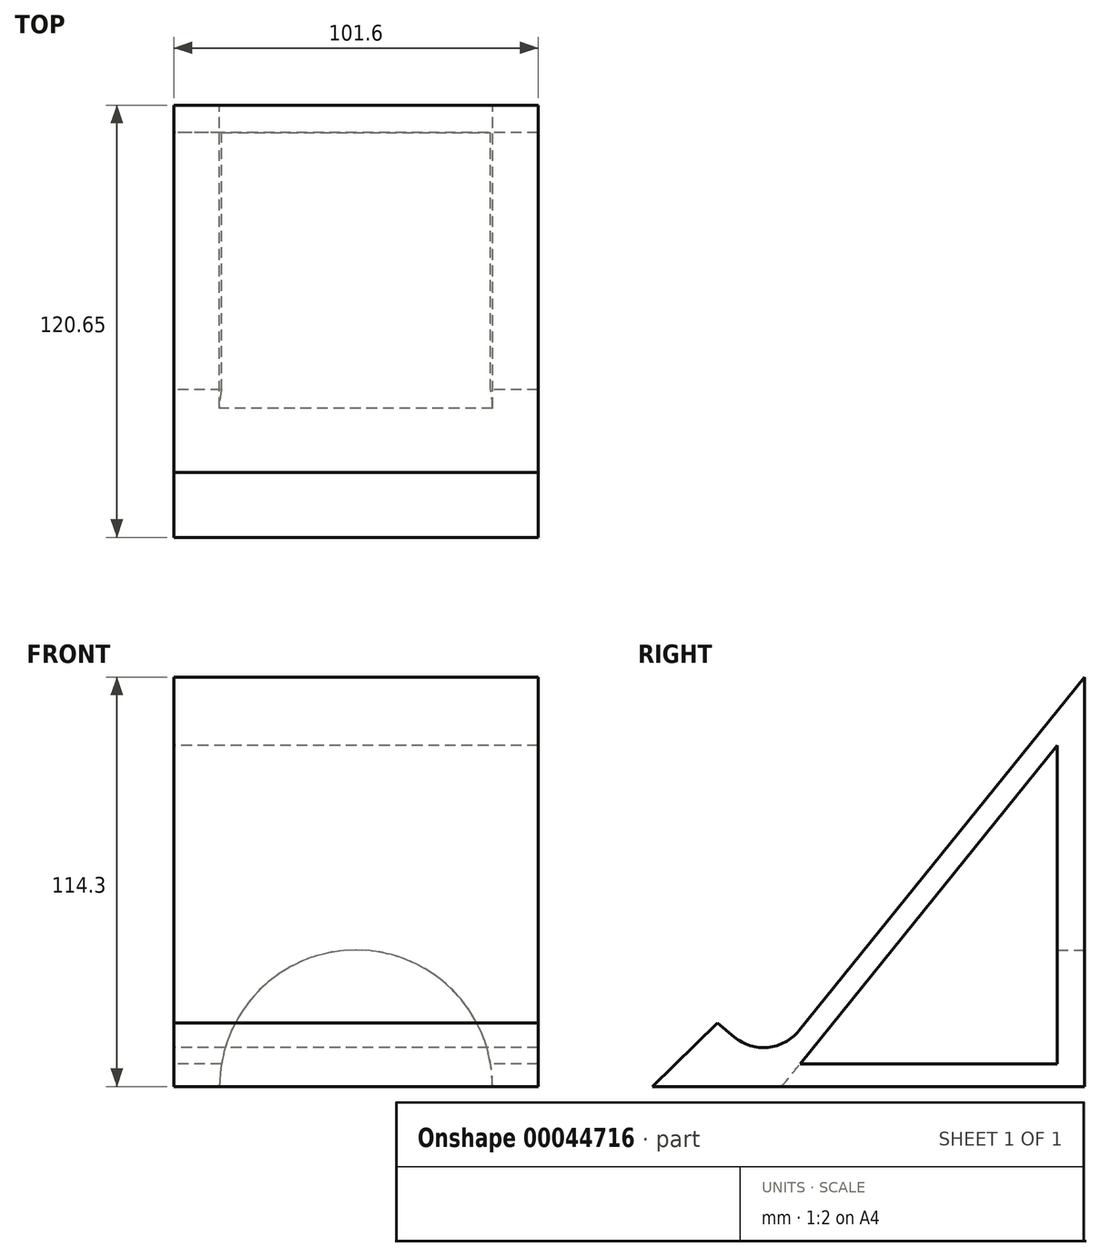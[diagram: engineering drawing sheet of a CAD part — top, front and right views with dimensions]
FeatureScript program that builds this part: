
annotation { "Feature Type Name" : "Feature", "Feature Type Description" : "" }
export const myFeature = defineFeature(function(context is Context, id is Id, definition is map)
    precondition{}
    {
        {
            var Q0;
            Q0=qCreatedBy(makeId("Right.planeOp"),FACE);
            var sketch = newSketch(context, id + "F0", { "sketchPlane" : qUnion([Q0])});
            skLineSegment(sketch, "E0", {"start": v(-54.33, -41.01) * mm, "end": v(66.32, -41.01) * mm});
            skLineSegment(sketch, "E1", {"start": v(66.32, -41.01) * mm, "end": v(66.32, 73.29) * mm});
            skLineSegment(sketch, "E2", {"start": v(-54.33, -41.01) * mm, "end": v(-36.18, -23.25) * mm});
            skLineSegment(sketch, "E3", {"start": v(-36.18, -23.25) * mm, "end": v(-31.51, -27.17) * mm});
            skLineSegment(sketch, "E4", {"start": v(-13.46, -25.44) * mm, "end": v(66.32, 73.29) * mm});
            skPoint(sketch, "E5.visualSharp", {"position": v(-21.6, -35.51) * mm});
            skArc(sketch, "E5.filletArc", {"start": v(-31.51, -27.17) * mm, "mid": v(-22.12, -30.1) * mm, "end": v(-13.46, -25.44) * mm});
            skLineSegment(sketch, "E6", {"start": v(-13.14, -34.66) * mm, "end": v(58.7, 54.24) * mm});
            skLineSegment(sketch, "E7", {"start": v(58.7, 54.24) * mm, "end": v(58.7, -34.66) * mm});
            skLineSegment(sketch, "E8", {"start": v(-13.14, -34.66) * mm, "end": v(58.7, -34.66) * mm});
            skLineSegment(sketch, "E9", {"start": v(58.7, 54.24) * mm, "end": v(66.32, 54.24) * mm});
            skLineSegment(sketch, "E10", {"start": v(58.7, -34.66) * mm, "end": v(58.7, -41.01) * mm});
            skSolve(sketch);
        }
        {
            var Q0;
            Q0 = qSketchRegion(id + "F0", true);
            extrude(context, id + "F1", {"entities" : qUnion([Q0]), "depth" : 101.6 * mm});
        }
        {
            var Q0;
            Q0=makeQuery(id+"F1.opExtrude","SWEPT_FACE",FACE,{"disambiguationData":[OSD([sQuery(id+"F0.wireOp",EDGE,"E1")])]});
            var sketch = newSketch(context, id + "F2", { "sketchPlane" : qUnion([Q0])});
            skArc(sketch, "E11", {"start": v(-12.7, -41.01) * mm, "mid": v(-50.8, -2.91) * mm, "end": v(-88.9, -41.01) * mm});
            skLineSegment(sketch, "E12", {"start": v(-88.9, -41.01) * mm, "end": v(-12.7, -41.01) * mm});
            skLineSegment(sketch, "E13", {"start": v(-88.9, -41.01) * mm, "end": v(-88.9, 73.29) * mm});
            skLineSegment(sketch, "E14", {"start": v(-12.7, -41.01) * mm, "end": v(-12.7, 73.29) * mm});
            skSolve(sketch);
        }
        {
            var Q0;
            Q0=makeQuery(id+"F2.imprint","IMPRINT",FACE,{"disambiguationData":[TD([[makeQuery(id+"F2.imprint","IMPRINT",EDGE,{"derivedFrom":sQuery(id+"F2.wireOp",EDGE,"E11")}),1.0]])]});
            var Q1;
            Q1=makeQuery(id+"F1.opExtrude","SWEPT_FACE",FACE,{"disambiguationData":[OSD([sQuery(id+"F0.wireOp",EDGE,"E6")])]});
            extrude(context, id + "F3", {"entities" : qUnion([Q0]), "operationType" : NewBodyOperationType.REMOVE, "endBound" : BoundingType.UP_TO_SURFACE, "oppositeDirection" : true, "endBoundEntityFace" : qUnion([Q1]), "depth" : 25.4 * mm});
        }
    });
